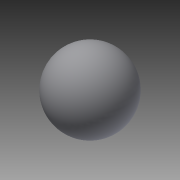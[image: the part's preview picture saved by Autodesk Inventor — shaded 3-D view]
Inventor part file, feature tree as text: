
AUTODESK INVENTOR PART (.ipt)
format: ipt  version: 2013 (Build 170138000, 138)  size: 96,256 bytes
history: native  units: in
note: dims shown in document units (in); Inventor stores cm internally (conversion verified against a paired STEP export)
features: revolve x1, sketch x1
ambient origin geometry x8: Origin, YZ Plane, XZ Plane, XY Plane, X Axis, Y Axis, Z Axis, Center Point
bodies: Solid1 (feature_tree)
feature tree (2):
  revolve  "Revolution1"  Angle=180.0deg
  sketch  "Sketch2"  dims[d1=24.0in d2=180.0deg]
